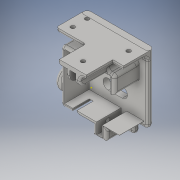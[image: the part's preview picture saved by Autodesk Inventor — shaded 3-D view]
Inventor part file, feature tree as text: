
AUTODESK INVENTOR PART (.ipt)
format: ipt  version: 2016 (Build 200138000, 138)  size: 990,208 bytes
history: native  units: in
note: dims shown in document units (in); Inventor stores cm internally (conversion verified against a paired STEP export)
features: sketch x18, fillet x18, extrude x14, plane x5, hole x3
ambient origin geometry x8: Origin, YZ Plane, XZ Plane, XY Plane, X Axis, Y Axis, Z Axis, Center Point
bodies: Solid1 (feature_tree)
feature tree (58):
  extrude  "Extrusion1"  Depth=0.8976in
  sketch  "Sketch12"  dims[d11=0.0787in d12=0.0787in d13=0.0787in d14=0.0787in d82=0.9016in d83=0.8858in]
  plane  "Work Plane6"
  extrude  "Extrusion5"  Depth=0.0787in
  plane  "Work Plane5"
  hole  "Hole3"  [1 undecoded]
  plane  "Work Plane1"
  extrude  "Extrusion6"  Depth=0.6142in
  extrude  "Extrusion7"  Depth=0.1614in
  plane  "Work Plane4"
  extrude  "Extrusion8"  Depth=0.2165in
  fillet  "Fillet15"  Radius=0.2165in
  plane  "Work Plane3"
  extrude  "Extrusion10"  Depth=0.0787in
  extrude  "Extrusion12"  Depth=0.0787in
  extrude  "Extrusion13"  Depth=0.0787in
  hole  "Hole4"  [1 undecoded]
  extrude  "Extrusion14"  Depth=0.0394in
  extrude  "Extrusion15"  Depth=0.0394in
  fillet  "Fillet19"  Radius=0.1575in
  fillet  "Fillet20"  Radius=0.0787in
  fillet  "Fillet22"  Radius=0.0787in
  fillet  "Fillet23"  Radius=0.0394in
  fillet  "Fillet24"  Radius=0.9016in
  fillet  "Fillet26"  Radius=0.1378in
  sketch  "Sketch37"  dims[d133=0.2165in d136=0.0787in]
  fillet  "Fillet29"  Radius=0.185in
  fillet  "Fillet30"  Radius=0.3543in
  extrude  "Extrusion16"  Depth=0.0787in
  hole  "Hole5"  [1 undecoded]
  extrude  "Extrusion18"  Depth=0.0394in
  fillet  "Fillet33"  Radius=0.0394in
  fillet  "Fillet36"  Radius=0.2717in
  fillet  "Fillet38"  Radius=0.2323in
  fillet  "Fillet39"  Radius=0.2835in
  fillet  "Fillet40"  Radius=0.4016in
  extrude  "Extrusion19"  Depth=0.3937in TaperAngle=0.0deg
  fillet  "Fillet41"  Radius=0.0787in
  fillet  "Fillet42"  Radius=0.0669in
  fillet  "Fillet43"  Radius=0.0906in
  extrude  "Extrusion20"  Depth=0.0787in
  fillet  "Fillet44"  Radius=0.1772in
  sketch  "Sketch1"  dims[d2=0.1181in d3=0.0in d6=0.8976in d9=0.357in d10=0.7139in]
  sketch  "Sketch14"  dims[d85=0.1102in d86=0.1102in]
  sketch  "Sketch17"  dims[d87=0.6142in d88=0.6142in]
  sketch  "Sketch18"  dims[d89=0.1614in d90=0.1614in]
  sketch  "Sketch22"  dims[d91=0.2992in d92=0.2165in d93=0.2165in]
  sketch  "Sketch24"  dims[d95=0.9016in d97=0.0787in]
  sketch  "Sketch30"  dims[d98=0.0787in d100=0.0787in]
  sketch  "Sketch32"  dims[d101=0.0787in d102=0.0787in]
  sketch  "Sketch33"  dims[d103=0.1693in d105=0.0787in]
  sketch  "Sketch35"  dims[d106=0.0394in d107=0.0394in]
  sketch  "Sketch36"  dims[d108=0.0394in d109=0.0394in d110=0.1575in d111=0.0787in d112=0.0787in d113=0.0394in d114=0.9016in d125=0.1378in d130=0.185in d132=0.3543in]
  sketch  "Sketch38"  dims[d137=0.315in d138=0.0in d139=0.0394in]
  sketch  "Sketch40"  dims[d144=0.0394in d145=0.7461in d146=0.0394in]
  sketch  "Sketch41"  dims[d147=0.07in d148=0.2362in d149=0.119in d150=0.0787in d151=0.5635in d152=0.315in d153=0.8108in d156=0.2717in d157=0.2323in d158=0.2835in d159=0.4016in]
  sketch  "Sketch42"  dims[d160=0.1575in d161=0.0in d164=0.3937in d165=0.0in d166=0.0787in d167=0.0in d171=0.0669in d177=0.0906in d178=0.0in]
  sketch  "Sketch43"  dims[d181=0.0787in d182=0.0787in d185=0.1772in d186=0.0483in d187=0.1063in d188=0.4724in d189=0.0in d190=0.3135in d191=0.4724in d192=0.0in d194=0.2559in d195=0.0394in d196=0.2559in d197=0.0394in d198=0.0787in d199=0.2362in d200=0.1575in d201=0.0787in d202=90.0deg d203=0.315in d204=0.8108in d205=0.1575in d206=0.0in d207=0.0394in d208=0.3937in d209=0.0in d210=0.0787in d211=0.0787in d213=0.0787in d214=0.0591in d215=0.0591in d217=0.0157in d220=0.0591in d221=0.0591in d222=0.5197in d223=0.126in d224=0.126in d225=0.5118in d226=0.0in d236=0.1575in d237=0.1575in d239=0.1969in d240=0.2953in d241=0.2953in d242=0.1969in d243=0.2598in d244=0.2598in d245=0.0787in d246=0.2362in d247=0.1575in d248=0.0787in d249=90.0deg d250=0.1181in d251=0.8108in d252=0.0197in d253=0.0in d254=0.0787in d257=0.0591in d259=0.0512in d260=0.0512in d261=0.0512in d262=0.5118in d263=0.0in d264=0.0984in d265=0.0394in d266=0.1181in d267=0.1969in d268=0.1969in d269=0.1575in d270=0.1575in d271=0.3937in d272=0.0in d273=0.0394in d274=0.1575in d275=0.1575in d26=0.0394in d27=0.0394in]
note: 3 required parameter values undecoded (feature->parameter linkage not recoverable at this tier; creation-order binding heuristic only, values carry confidence <= 0.55)
